# Revit family: Saxi Teanik Spärrnät
name_source: partatom
category: Mechanical Equipment
revit_build: Autodesk Revit Architecture 2015 (Build: 20140322_1515(x64)
units: mm (PartAtom-declared; Revit-internal decimal feet)

## types (1)
- Saxi Teanik Spärrnät
    Bracket_Height_OMV = 7650 mm  [stored 25.0984 ft]
    Bracket_Offset = 3000 mm  [stored 9.84252 ft]
    Brackets_Array_Visible = Yes
    Brackets_Single_Visible = No
    First_Bracket = 9250 mm
    First_Bracket_From_Edge = 250 mm  [stored 0.82021 ft]
    Last_Bracket = 21250 mm
    Machinery_Height = 7750 mm  [stored 25.4265 ft]
    Manufacturer = Saxi Vägg AB
    Model = Saxi Teanik Spärrnät
    Motor_Height_OMV = 7833 mm  [stored 25.6988 ft]
    Motor_Placement = 10675 mm  [stored 35.023 ft]
    NO_Brackets = 3
    NO_brackets_REAL = 3
    Net_Height = 6970 mm
    Shaft_Legth = 21350 mm  [stored 70.0459 ft]
    Tissue_Height = 7000 mm  [stored 22.9659 ft]
    To_Shaft = 7795 mm  [stored 25.5741 ft]
    UK_Upphissad = 7000 mm  [stored 22.9659 ft]
    URL = http://www.saxi.se
    Width = 21500 mm

note: [stored X ft] marks values corroborated as IEEE doubles in the binary element streams (Revit-internal decimal feet)

## geometry (parser evidence)
native form markers: Sweep x12
no freeform markers — native parametric forms only
